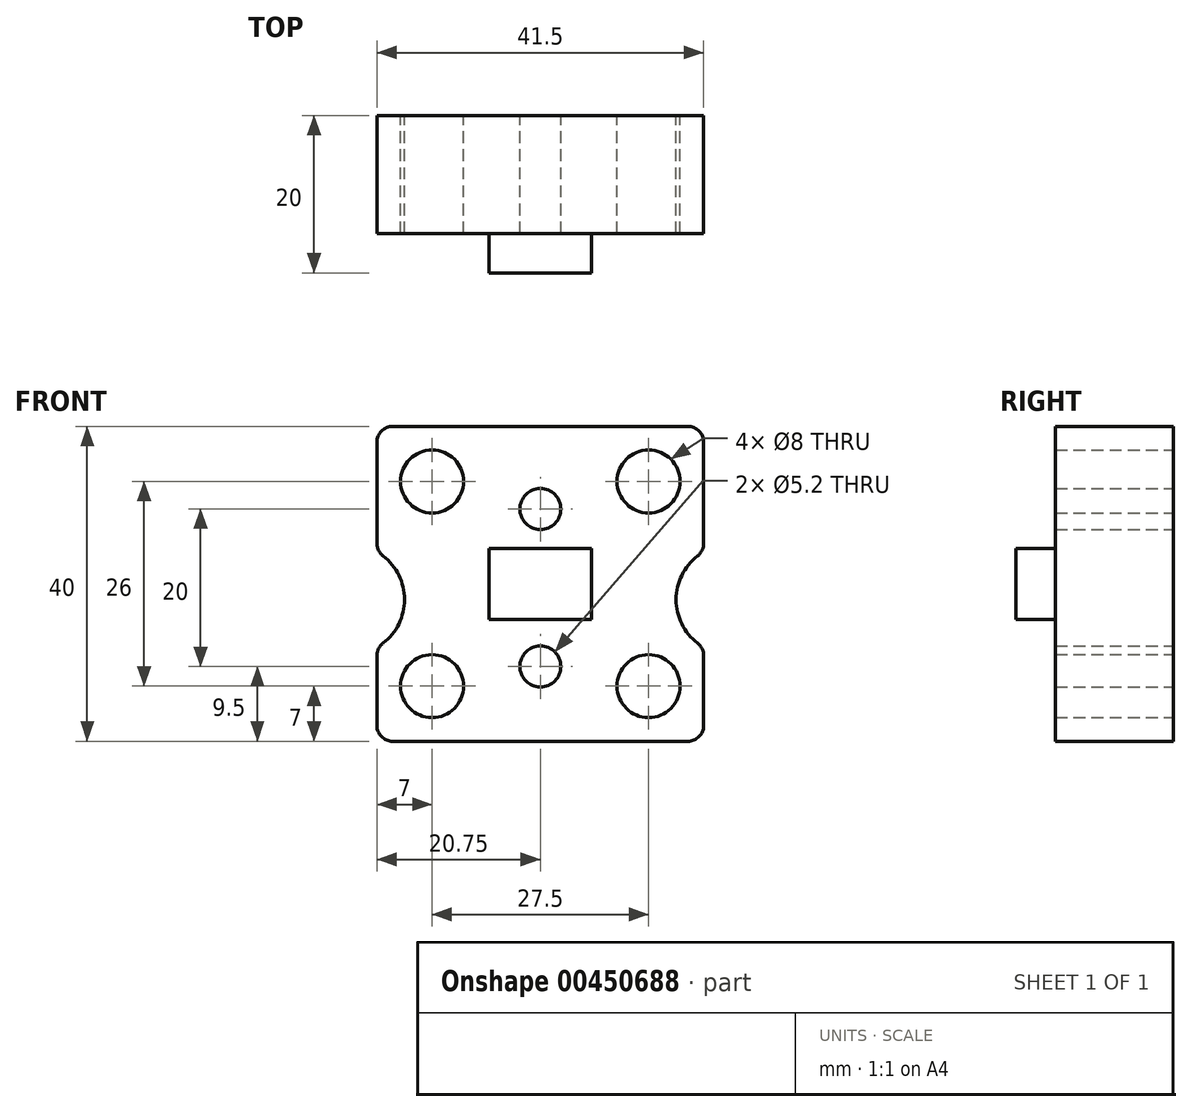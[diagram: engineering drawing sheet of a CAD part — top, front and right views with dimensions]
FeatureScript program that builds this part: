
annotation { "Feature Type Name" : "Feature", "Feature Type Description" : "" }
export const myFeature = defineFeature(function(context is Context, id is Id, definition is map)
    precondition{}
    {
        {
            var Q0;
            Q0=qCreatedBy(makeId("Front.planeOp"),FACE);
            var sketch = newSketch(context, id + "F0", { "sketchPlane" : qUnion([Q0])});
            skLineSegment(sketch, "E0.bottom", {"start": v(-20.75, 22) * mm, "end": v(20.75, 22) * mm});
            skLineSegment(sketch, "E0.top", {"start": v(-20.75, -18) * mm, "end": v(20.75, -18) * mm});
            skLineSegment(sketch, "E0.left", {"start": v(-20.75, 22) * mm, "end": v(-20.75, 6.06) * mm});
            skLineSegment(sketch, "E0.right", {"start": v(20.75, 22) * mm, "end": v(20.75, 6.06) * mm});
            skCircle(sketch, "E1", {"center": v(0, 11.5) * mm, "radius": 2.6 * mm});
            skCircle(sketch, "E2", {"center": v(0, -8.5) * mm, "radius": 2.6 * mm});
            skArc(sketch, "E3", {"start": v(20.75, 6.06) * mm, "mid": v(17.25, 0) * mm, "end": v(20.75, -6.06) * mm});
            skArc(sketch, "E4", {"start": v(-20.75, -6.06) * mm, "mid": v(-17.25, 0) * mm, "end": v(-20.75, 6.06) * mm});
            skLineSegment(sketch, "E5.trimOffspring", {"start": v(-20.75, -6.06) * mm, "end": v(-20.75, -18) * mm});
            skLineSegment(sketch, "E6.trimOffspring", {"start": v(20.75, -6.06) * mm, "end": v(20.75, -18) * mm});
            skCircle(sketch, "E7", {"center": v(-13.75, -11) * mm, "radius": 4 * mm});
            skCircle(sketch, "E8.0.1.0", {"center": v(-13.75, 15) * mm, "radius": 4 * mm});
            skCircle(sketch, "E8.1.0.0", {"center": v(13.75, -11) * mm, "radius": 4 * mm});
            skCircle(sketch, "E8.1.1.0", {"center": v(13.75, 15) * mm, "radius": 4 * mm});
            skLineSegment(sketch, "E8.direction1", {"start": v(-13.75, -11) * mm, "end": v(13.75, -11) * mm, "construction": true});
            skLineSegment(sketch, "E8.direction2", {"start": v(-13.75, -11) * mm, "end": v(-13.75, 15) * mm, "construction": true});
            skSolve(sketch);
        }
        {
            var Q0;
            Q0=makeQuery(id+"F0.imprint","IMPRINT",FACE,{"disambiguationData":[TD([[makeQuery(id+"F0.imprint","IMPRINT",EDGE,{"derivedFrom":sQuery(id+"F0.wireOp",EDGE,"E0.bottom")}),-1.0]])]});
            extrude(context, id + "F1", {"entities" : qUnion([Q0]), "depth" : 15 * mm});
        }
        {
            var Q0;
            Q0=makeQuery(id+"F1.opExtrude","SWEPT_EDGE",EDGE,{"disambiguationData":[OSD([sQuery(id+"F0.wireOp",EDGE,"E0.bottom"),sQuery(id+"F0.wireOp",EDGE,"E0.left")])]});
            var Q1;
            Q1=makeQuery(id+"F1.opExtrude","SWEPT_EDGE",EDGE,{"disambiguationData":[OSD([sQuery(id+"F0.wireOp",EDGE,"E0.bottom"),sQuery(id+"F0.wireOp",EDGE,"E0.right")])]});
            var Q2;
            Q2=makeQuery(id+"F1.opExtrude","SWEPT_EDGE",EDGE,{"disambiguationData":[OSD([sQuery(id+"F0.wireOp",EDGE,"E0.top"),sQuery(id+"F0.wireOp",EDGE,"E5.trimOffspring")])]});
            var Q3;
            Q3=makeQuery(id+"F1.opExtrude","SWEPT_EDGE",EDGE,{"disambiguationData":[OSD([sQuery(id+"F0.wireOp",EDGE,"E0.top"),sQuery(id+"F0.wireOp",EDGE,"E6.trimOffspring")])]});
            var Q4;
            Q4=makeQuery(id+"F1.opExtrude","SWEPT_EDGE",EDGE,{"disambiguationData":[OSD([sQuery(id+"F0.wireOp",EDGE,"E0.right"),sQuery(id+"F0.wireOp",EDGE,"E3")])]});
            var Q5;
            Q5=makeQuery(id+"F1.opExtrude","SWEPT_EDGE",EDGE,{"disambiguationData":[OSD([sQuery(id+"F0.wireOp",EDGE,"E3"),sQuery(id+"F0.wireOp",EDGE,"E6.trimOffspring")])]});
            var Q6;
            Q6=makeQuery(id+"F1.opExtrude","SWEPT_EDGE",EDGE,{"disambiguationData":[OSD([sQuery(id+"F0.wireOp",EDGE,"E0.left"),sQuery(id+"F0.wireOp",EDGE,"E4")])]});
            var Q7;
            Q7=makeQuery(id+"F1.opExtrude","SWEPT_EDGE",EDGE,{"disambiguationData":[OSD([sQuery(id+"F0.wireOp",EDGE,"E4"),sQuery(id+"F0.wireOp",EDGE,"E5.trimOffspring")])]});
            fillet(context, id + "F2", {"entities" : qUnion([Q0, Q1, Q2, Q3, Q4, Q5, Q6, Q7]), "radius" : 2 * mm, "tangentPropagation" : true, "allowEdgeOverflow" : false});
        }
        {
            var Q0;
            Q0=makeQuery(id+"F1.opExtrude","CAP_FACE",FACE,{"disambiguationData":[OSD([sQuery(id+"F0.wireOp",EDGE,"E0.bottom"),sQuery(id+"F0.wireOp",EDGE,"E0.top"),sQuery(id+"F0.wireOp",EDGE,"E0.left"),sQuery(id+"F0.wireOp",EDGE,"E0.right"),sQuery(id+"F0.wireOp",EDGE,"E1"),sQuery(id+"F0.wireOp",EDGE,"E2"),sQuery(id+"F0.wireOp",EDGE,"E3"),sQuery(id+"F0.wireOp",EDGE,"E4"),sQuery(id+"F0.wireOp",EDGE,"E5.trimOffspring"),sQuery(id+"F0.wireOp",EDGE,"E6.trimOffspring"),sQuery(id+"F0.wireOp",EDGE,"E7"),sQuery(id+"F0.wireOp",EDGE,"E8.0.1.0"),sQuery(id+"F0.wireOp",EDGE,"E8.1.0.0"),sQuery(id+"F0.wireOp",EDGE,"E8.1.1.0")])],"isStart":false});
            var sketch = newSketch(context, id + "F3", { "sketchPlane" : qUnion([Q0])});
            skLineSegment(sketch, "E9.bottom", {"start": v(-6.5, 6.5) * mm, "end": v(6.5, 6.5) * mm});
            skLineSegment(sketch, "E9.top", {"start": v(-6.5, -2.5) * mm, "end": v(6.5, -2.5) * mm});
            skLineSegment(sketch, "E9.left", {"start": v(-6.5, 6.5) * mm, "end": v(-6.5, -2.5) * mm});
            skLineSegment(sketch, "E9.right", {"start": v(6.5, 6.5) * mm, "end": v(6.5, -2.5) * mm});
            skSolve(sketch);
        }
        {
            var Q0;
            Q0=makeQuery(id+"F3.imprint","IMPRINT",FACE,{"disambiguationData":[TD([[makeQuery(id+"F3.imprint","IMPRINT",EDGE,{"derivedFrom":sQuery(id+"F3.wireOp",EDGE,"E9.bottom")}),-1.0]])]});
            extrude(context, id + "F4", {"entities" : qUnion([Q0]), "operationType" : NewBodyOperationType.ADD, "depth" : 5 * mm});
        }
    });
